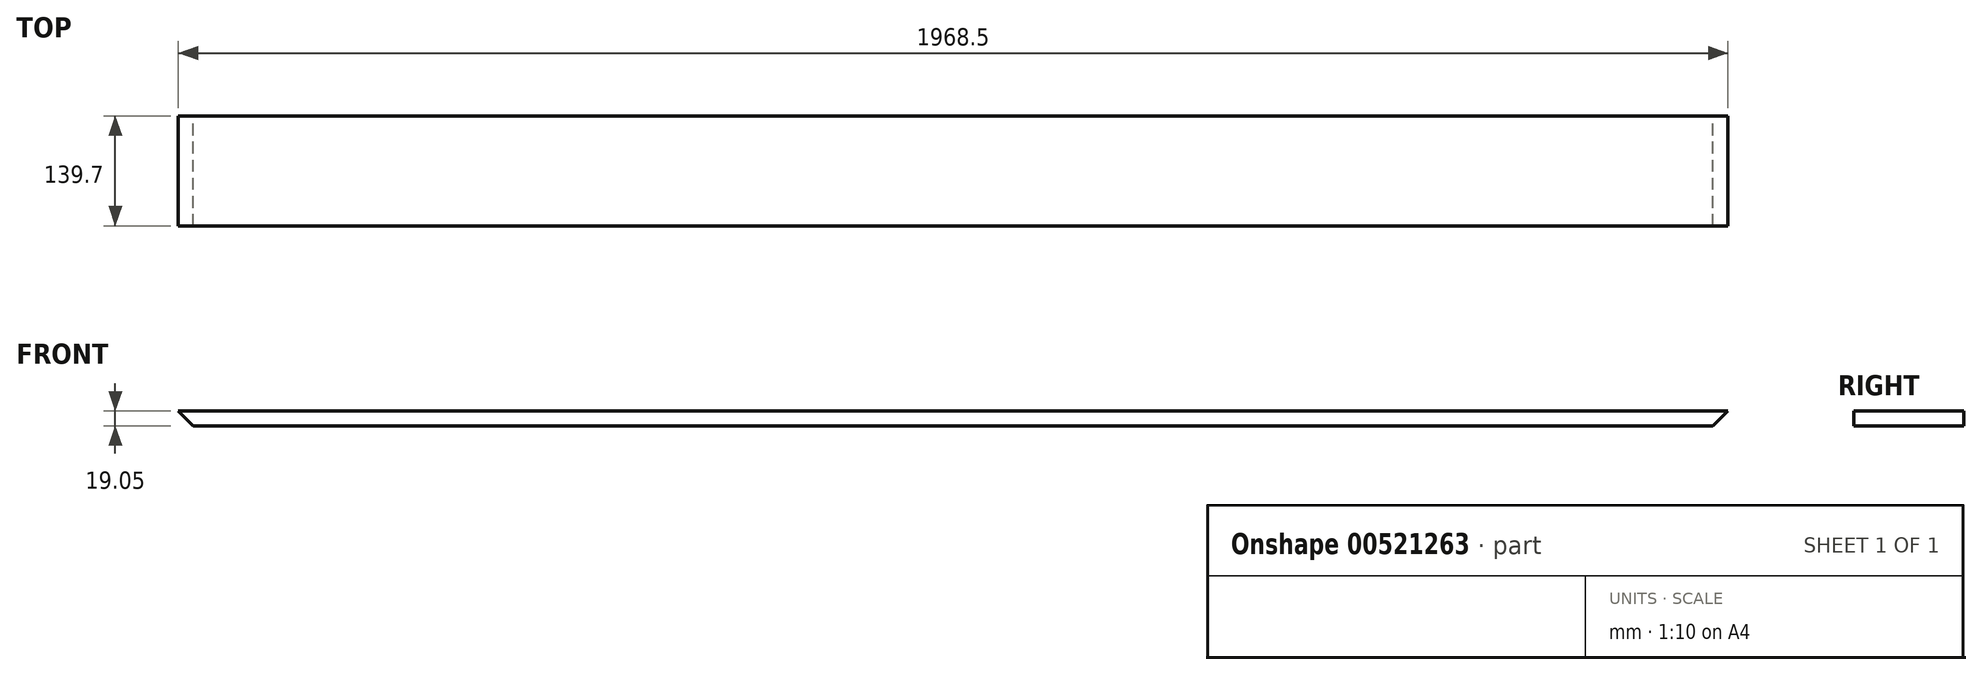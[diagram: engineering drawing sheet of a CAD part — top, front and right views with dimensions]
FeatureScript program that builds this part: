
annotation { "Feature Type Name" : "Feature", "Feature Type Description" : "" }
export const myFeature = defineFeature(function(context is Context, id is Id, definition is map)
    precondition{}
    {
        {
            var Q0;
            Q0=qCreatedBy(makeId("Front.planeOp"),FACE);
            var sketch = newSketch(context, id + "F0", { "sketchPlane" : qUnion([Q0])});
            skLineSegment(sketch, "E0", {"start": v(-965.2, 0) * mm, "end": v(-984.25, 19.05) * mm});
            skLineSegment(sketch, "E1", {"start": v(-984.25, 19.05) * mm, "end": v(984.25, 19.05) * mm});
            skLineSegment(sketch, "E2", {"start": v(984.25, 19.05) * mm, "end": v(965.2, 0) * mm});
            skLineSegment(sketch, "E3", {"start": v(965.2, 0) * mm, "end": v(-965.2, 0) * mm});
            skLineSegment(sketch, "E4", {"start": v(0, 570.25) * mm, "end": v(0, -656.25) * mm});
            skLineSegment(sketch, "E5", {"start": v(-542.33, 0) * mm, "end": v(651.2, 0) * mm});
            skSolve(sketch);
        }
        {
            var Q0;
            {var subQ0=sQuery(id+"F0.wireOp",EDGE,"E2");Q0=makeQuery(id+"F0.imprint","IMPRINT",FACE,{"disambiguationData":[TD([[makeQuery(id+"F0.imprint","IMPRINT",EDGE,{"derivedFrom":subQ0}),-1.0]])]});}
            var Q1;
            {var subQ0=sQuery(id+"F0.wireOp",EDGE,"E0");Q1=makeQuery(id+"F0.imprint","IMPRINT",FACE,{"disambiguationData":[TD([[makeQuery(id+"F0.imprint","IMPRINT",EDGE,{"derivedFrom":subQ0}),-1.0]])]});}
            extrude(context, id + "F1", {"entities" : qUnion([Q0, Q1]), "depth" : 139.7 * mm, "offsetDistance" : 25.4 * mm});
        }
    });
